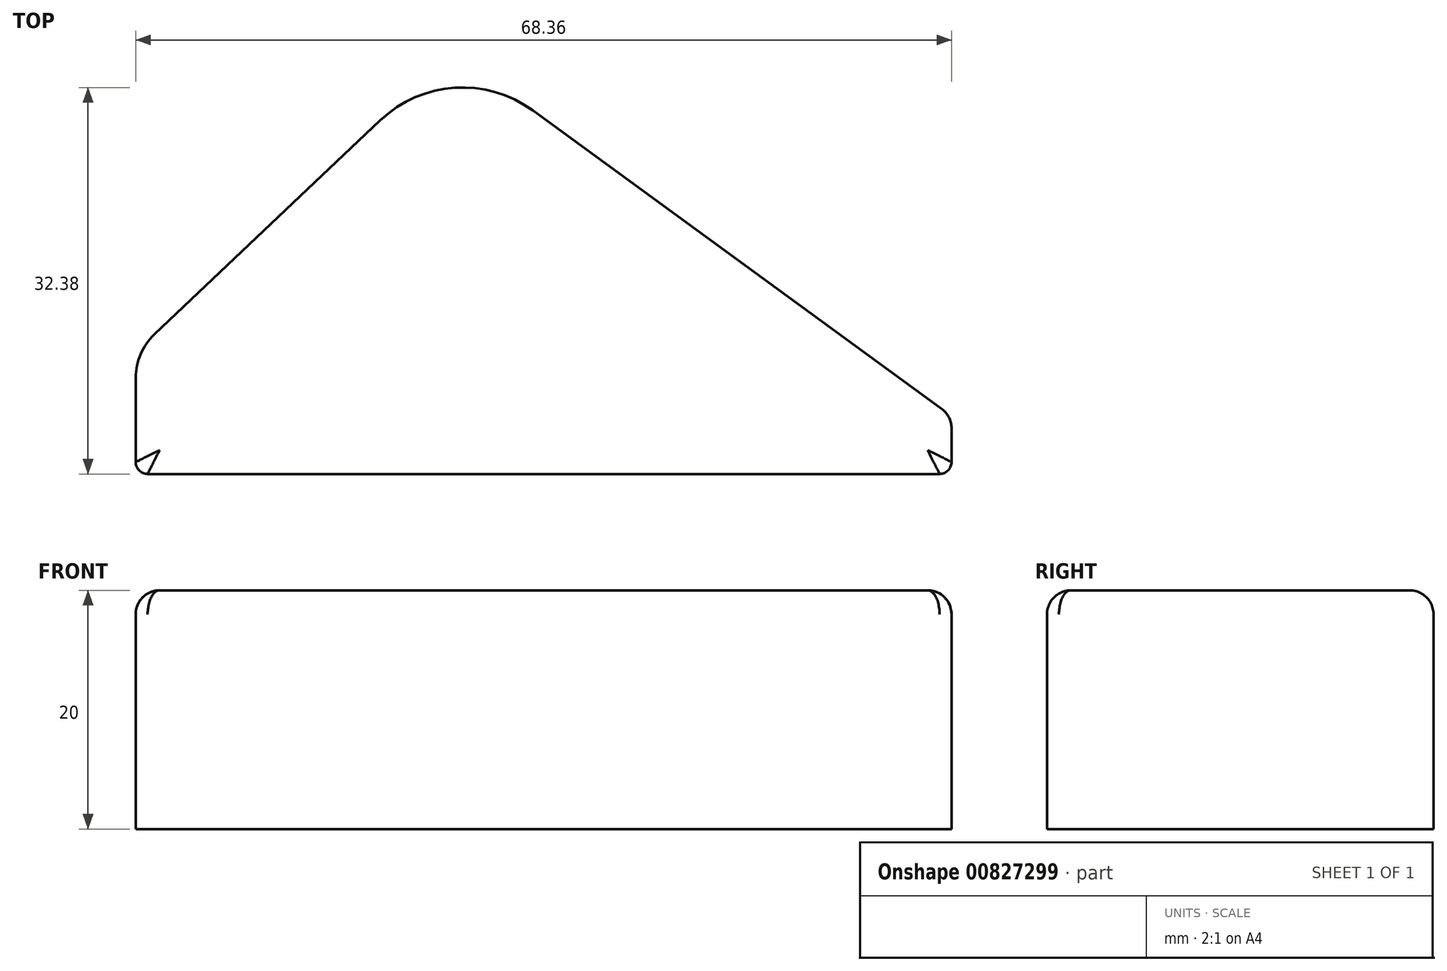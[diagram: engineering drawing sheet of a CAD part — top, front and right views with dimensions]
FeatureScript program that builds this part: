
annotation { "Feature Type Name" : "Feature", "Feature Type Description" : "" }
export const myFeature = defineFeature(function(context is Context, id is Id, definition is map)
    precondition{}
    {
        {
            var Q0;
            Q0=qCreatedBy(makeId("Top.planeOp"),FACE);
            var sketch = newSketch(context, id + "F0", { "sketchPlane" : qUnion([Q0])});
            skLineSegment(sketch, "E0", {"start": v(-34, 25) * mm, "end": v(-8.46, 25) * mm});
            skLineSegment(sketch, "E1", {"start": v(32.36, 25) * mm, "end": v(-8.46, 25) * mm});
            skLineSegment(sketch, "E2", {"start": v(-8.46, 25) * mm, "end": v(-8.46, 60.37) * mm});
            skLineSegment(sketch, "E3", {"start": v(-35, 26) * mm, "end": v(-35, 33.07) * mm});
            skLineSegment(sketch, "E4", {"start": v(-33.44, 36.7) * mm, "end": v(-14.5, 54.64) * mm});
            skLineSegment(sketch, "E5", {"start": v(-1.73, 55.46) * mm, "end": v(32.54, 30.45) * mm});
            skPoint(sketch, "E6.visualSharp", {"position": v(-35, 35.22) * mm});
            skArc(sketch, "E6.filletArc", {"start": v(-33.44, 36.7) * mm, "mid": v(-34.6, 35.04) * mm, "end": v(-35, 33.07) * mm});
            skPoint(sketch, "E7.visualSharp", {"position": v(-8.46, 60.37) * mm});
            skArc(sketch, "E7.filletArc", {"start": v(-1.73, 55.46) * mm, "mid": v(-8.27, 57.36) * mm, "end": v(-14.5, 54.64) * mm});
            skArc(sketch, "E8.filletArc", {"start": v(-35, 26) * mm, "mid": v(-34.7, 25.3) * mm, "end": v(-34, 25) * mm});
            skLineSegment(sketch, "E9", {"start": v(33.36, 26) * mm, "end": v(33.36, 28.83) * mm});
            skArc(sketch, "E10.filletArc", {"start": v(32.36, 25) * mm, "mid": v(33.07, 25.3) * mm, "end": v(33.36, 26) * mm});
            skPoint(sketch, "E11.visualSharp", {"position": v(33.36, 29.85) * mm});
            skArc(sketch, "E11.filletArc", {"start": v(33.36, 28.83) * mm, "mid": v(33.14, 29.74) * mm, "end": v(32.54, 30.45) * mm});
            skSolve(sketch);
        }
        {
            var Q0;
            {var subQ2=sQuery(id+"F0.wireOp",EDGE,"E0");Q0=makeQuery(id+"F0.imprint","IMPRINT",FACE,{"disambiguationData":[TD([[makeQuery(id+"F0.imprint","IMPRINT",EDGE,{"derivedFrom":subQ2}),1.0]])]});}
            var Q1;
            {var subQ1=sQuery(id+"F0.wireOp",EDGE,"E1");Q1=makeQuery(id+"F0.imprint","IMPRINT",FACE,{"disambiguationData":[TD([[makeQuery(id+"F0.imprint","IMPRINT",EDGE,{"derivedFrom":subQ1}),-1.0]])]});}
            extrude(context, id + "F1", {"entities" : qUnion([Q0, Q1]), "depth" : 20 * mm, "offsetDistance" : 25 * mm});
        }
        {
            var Q0;
            Q0=makeQuery(id+"F1.opExtrude","CAP_EDGE",EDGE,{"disambiguationData":[OSD([sQuery(id+"F0.wireOp",EDGE,"E0"),sQuery(id+"F0.wireOp",EDGE,"E1")])],"isStart":false});
            fillet(context, id + "F2", {"entities" : qUnion([Q0]), "radius" : 2 * mm, "tangentPropagation" : true, "allowEdgeOverflow" : false});
        }
    });
